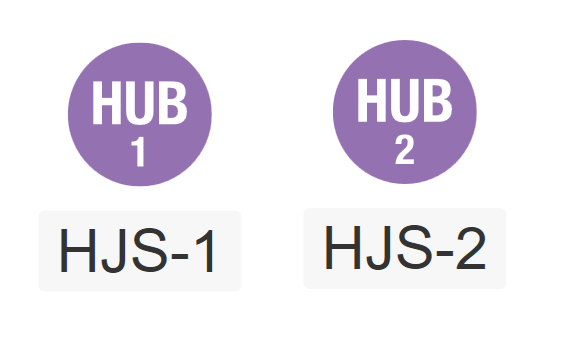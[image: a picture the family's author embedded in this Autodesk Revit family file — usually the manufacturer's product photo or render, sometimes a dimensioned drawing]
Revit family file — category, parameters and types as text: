
# Revit family: CSensor-Lutron-Ceiling-Vive_Series-HJS-2-SM
name_source: partatom
category: Lighting Devices
units: mm (PartAtom-declared; Revit-internal decimal feet)

## family parameters
Cut with Voids When Loaded = No
Host = Face
Maintain Annotation Orientation = Yes
OmniClass Number = 23.85.80.11.27
OmniClass Title = Lighting Controls
Part Type = Normal
Room Calculation Point = No
Round Connector Dimension = Use Diameter
Shared = No

## types (1)
- HJS-2-SM
    Apparent Load = 0 VA
    Assembly Code = D5030800
    Cost = 0 $
    Coverage = 15836.00 SF
    Coverage Area = 360˚ coverage from 71 ft (22 m)
    Coverage Range = 71 ft (22 m)
    Coverge Radius = 71' - 0"
    Default Elevation = 0' - 0"
    Depth = 0' - 4 39/128"
    Description = Vive hub, surface-mount adapter and power supply
    Finish = Plastic - Lutron - White Gloss
    Instruction Sheet Link = https://assets.lutron.com
    Keynote = Division 11
    Length = 0' - 6 103/128"
    Load Classification = Other
    Manufacturer = Lutron Electronics Co., Inc
    Manufacturer Fax Number = 610-282-1243
    Maximum Operating Temperature = 104 °F
    Minimum Operating Temperature = 32 °F
    Model = HJS-2-SM
    Performance URL = https://www.lutron.com
    Product Documentation Link = https://assets.lutron.com
    Product Name = Premium Vive hub with BACnet
    Product Page URL = https://commercial.lutron.com
    Sensor Material = Plastic - Lutron - White Gloss
    Sensor Type = Occupancy/Vacancy
    Series = Vive Series
    URL = http://www.lutron.com
    Version = 2021 - v1.0a
    Video Link = https://www.youtube.com
    Voltage = 120 V
    Voltage Comments = Input to power supply: 120 – 277 V~ 50/60 Hz 0.6 A • Input to Vive hub: 24 V- 350 mA
    Warranty URL = https://www.lutron.com
    Width = 0' - 6 103/128"

## geometry (parser evidence)
native form markers: Sweep x5
no freeform markers — native parametric forms only
